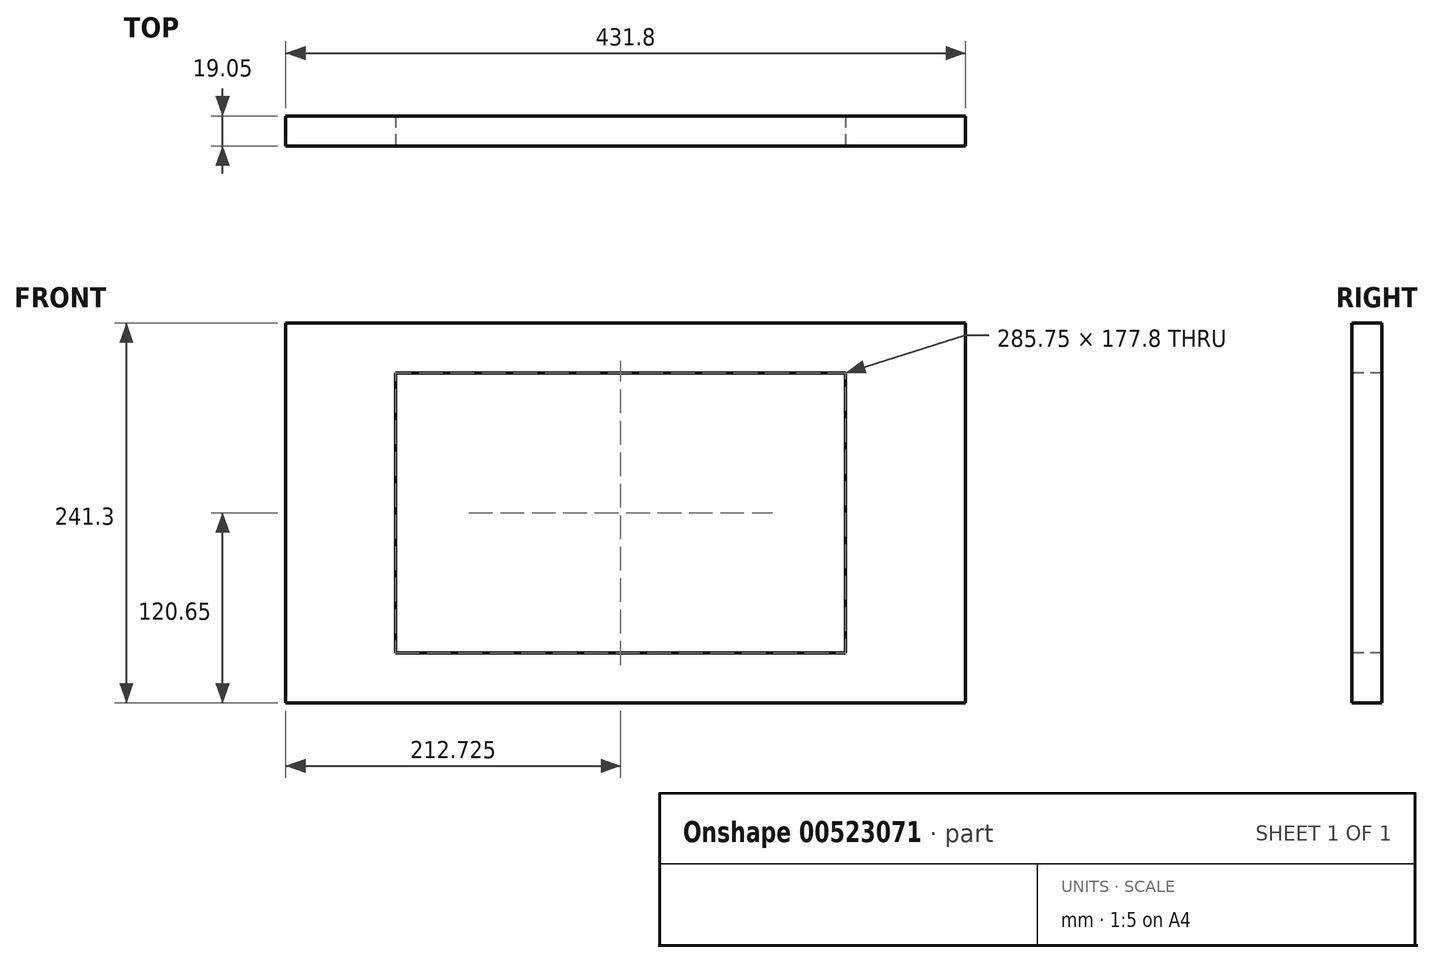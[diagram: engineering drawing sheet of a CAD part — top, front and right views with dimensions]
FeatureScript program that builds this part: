
annotation { "Feature Type Name" : "Feature", "Feature Type Description" : "" }
export const myFeature = defineFeature(function(context is Context, id is Id, definition is map)
    precondition{}
    {
        {
            var Q0;
            Q0=qCreatedBy(makeId("Front.planeOp"),FACE);
            var sketch = newSketch(context, id + "F0", { "sketchPlane" : qUnion([Q0])});
            skLineSegment(sketch, "E0.bottom", {"start": v(0, 0) * mm, "end": v(431.8, 0) * mm});
            skLineSegment(sketch, "E0.top", {"start": v(0, 241.3) * mm, "end": v(431.8, 241.3) * mm});
            skLineSegment(sketch, "E0.left", {"start": v(0, 0) * mm, "end": v(0, 241.3) * mm});
            skLineSegment(sketch, "E0.right", {"start": v(431.8, 0) * mm, "end": v(431.8, 241.3) * mm});
            skSolve(sketch);
        }
        {
            var Q0;
            Q0 = qSketchRegion(id + "F0", true);
            extrude(context, id + "F1", {"entities" : qUnion([Q0]), "depth" : 19.05 * mm, "offsetDistance" : 25.4 * mm});
        }
        {
            var Q0;
            Q0=makeQuery(id+"F1.opExtrude","CAP_FACE",FACE,{"disambiguationData":[OSD([sQuery(id+"F0.wireOp",EDGE,"E0.bottom"),sQuery(id+"F0.wireOp",EDGE,"E0.top"),sQuery(id+"F0.wireOp",EDGE,"E0.left"),sQuery(id+"F0.wireOp",EDGE,"E0.right")])],"isStart":false});
            var sketch = newSketch(context, id + "F2", { "sketchPlane" : qUnion([Q0])});
            skLineSegment(sketch, "E1.bottom", {"start": v(355.6, 209.55) * mm, "end": v(69.85, 209.55) * mm});
            skLineSegment(sketch, "E1.top", {"start": v(355.6, 31.75) * mm, "end": v(69.85, 31.75) * mm});
            skLineSegment(sketch, "E1.left", {"start": v(355.6, 209.55) * mm, "end": v(355.6, 31.75) * mm});
            skLineSegment(sketch, "E1.right", {"start": v(69.85, 209.55) * mm, "end": v(69.85, 31.75) * mm});
            skSolve(sketch);
        }
        {
            var Q0;
            Q0 = qSketchRegion(id + "F2", true);
            extrude(context, id + "F3", {"entities" : qUnion([Q0]), "operationType" : NewBodyOperationType.REMOVE, "endBound" : BoundingType.THROUGH_ALL, "oppositeDirection" : true, "depth" : 25.4 * mm, "offsetDistance" : 25.4 * mm});
        }
    });
